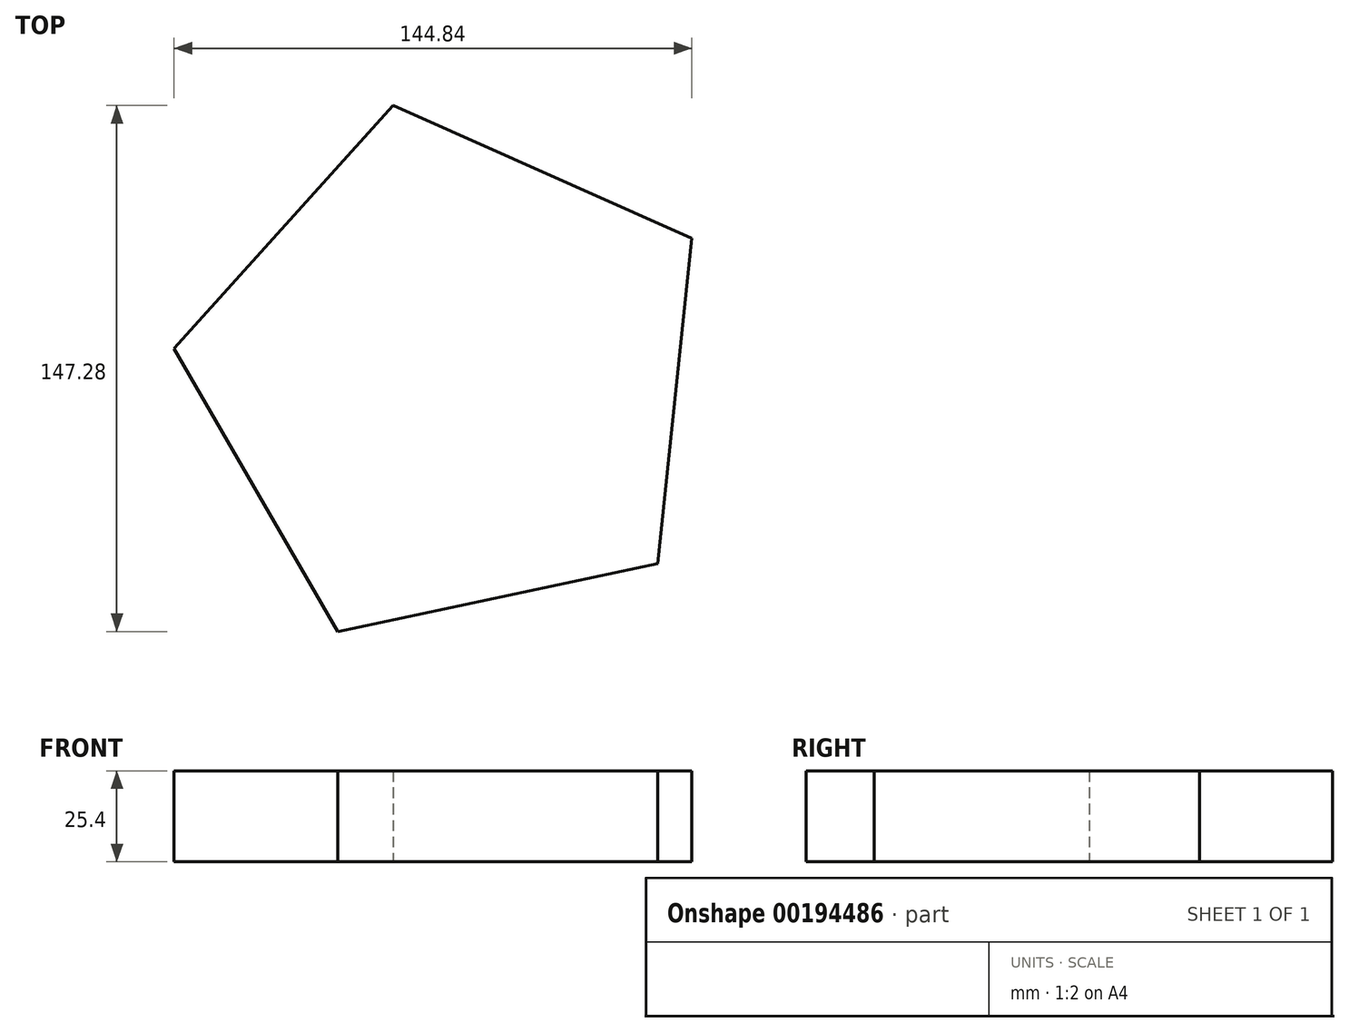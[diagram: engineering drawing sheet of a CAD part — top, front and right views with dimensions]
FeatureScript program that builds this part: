
annotation { "Feature Type Name" : "Feature", "Feature Type Description" : "" }
export const myFeature = defineFeature(function(context is Context, id is Id, definition is map)
    precondition{}
    {
        {
            var Q0;
            Q0=qCreatedBy(makeId("Top.planeOp"),FACE);
            var sketch = newSketch(context, id + "F0", { "sketchPlane" : qUnion([Q0])});
            skCircle(sketch, "E0.cCircle", {"center": v(0, 0) * mm, "radius": 62.98 * mm, "construction": true});
            skLineSegment(sketch, "E0.0", {"start": v(57.86, -52.08) * mm, "end": v(-31.65, -71.13) * mm});
            skLineSegment(sketch, "E0.1", {"start": v(-31.65, -71.13) * mm, "end": v(-77.43, 8.12) * mm});
            skLineSegment(sketch, "E0.2", {"start": v(-77.43, 8.12) * mm, "end": v(-16.2, 76.15) * mm});
            skLineSegment(sketch, "E0.3", {"start": v(-16.2, 76.15) * mm, "end": v(67.41, 38.94) * mm});
            skLineSegment(sketch, "E0.4", {"start": v(67.41, 38.94) * mm, "end": v(57.86, -52.08) * mm});
            skPoint(sketch, "E0.0.midPoint", {"position": v(13.1, -61.6) * mm});
            skSolve(sketch);
        }
        {
            var Q0;
            Q0=makeQuery(id+"F0.imprint","IMPRINT",FACE,{"disambiguationData":[TD([[makeQuery(id+"F0.imprint","IMPRINT",EDGE,{"derivedFrom":sQuery(id+"F0.wireOp",EDGE,"E0.0")}),-1.0]])]});
            extrude(context, id + "F1", {"entities" : qUnion([Q0]), "depth" : 25.4 * mm});
        }
    });
